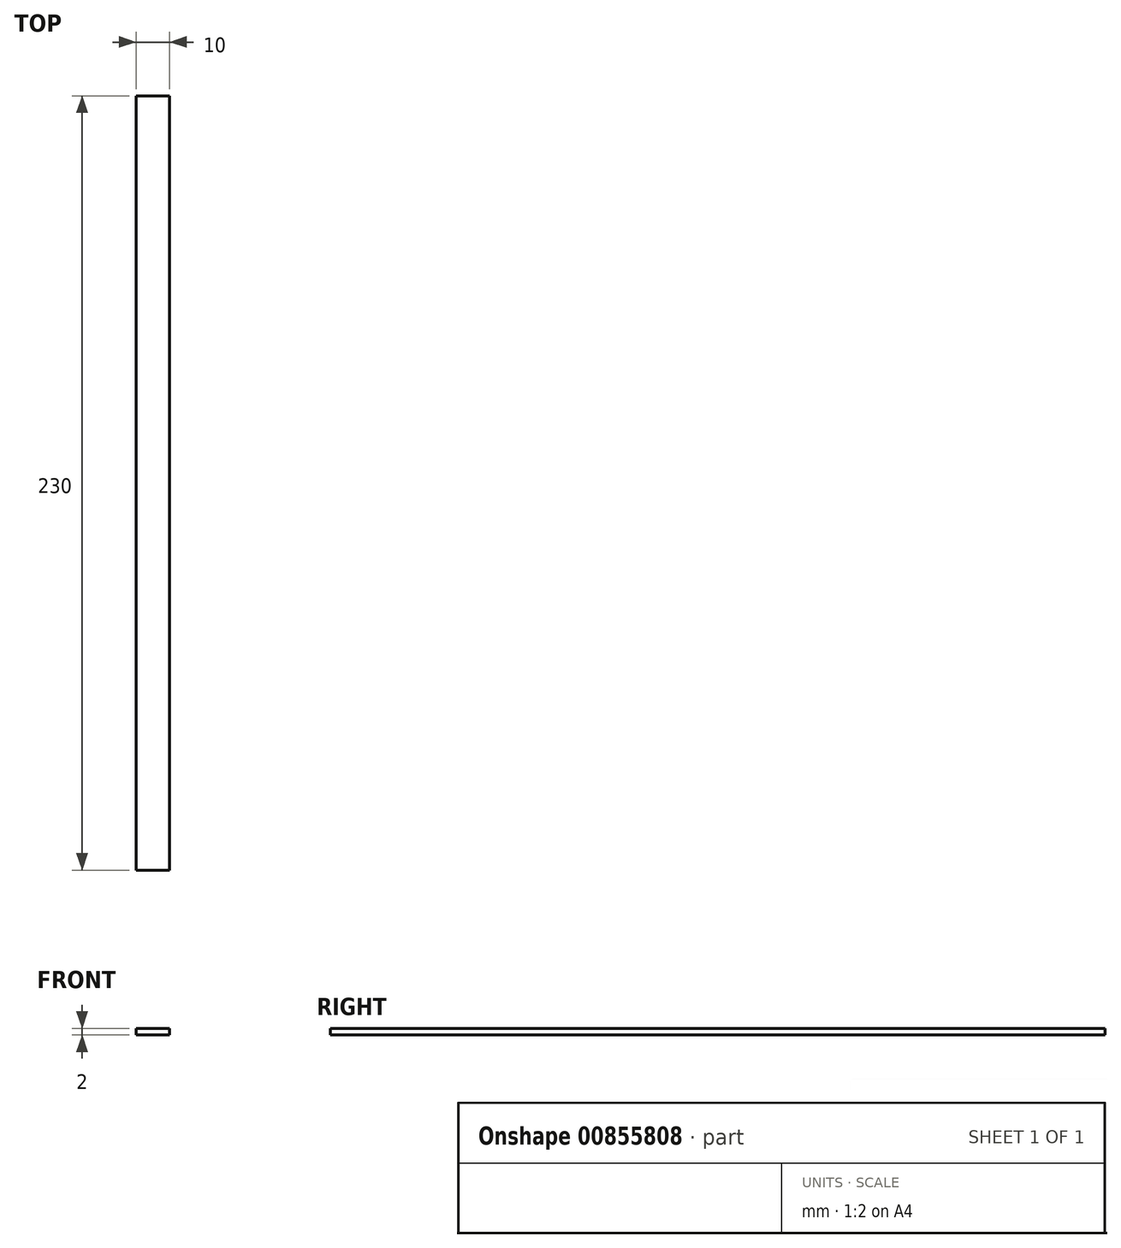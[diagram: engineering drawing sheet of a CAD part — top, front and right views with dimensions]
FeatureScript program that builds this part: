
annotation { "Feature Type Name" : "Feature", "Feature Type Description" : "" }
export const myFeature = defineFeature(function(context is Context, id is Id, definition is map)
    precondition{}
    {
        {
            var Q0;
            Q0=qCreatedBy(makeId("Front.planeOp"),FACE);
            var sketch = newSketch(context, id + "F0", { "sketchPlane" : qUnion([Q0])});
            skLineSegment(sketch, "E0.bottom", {"start": v(5, 1) * mm, "end": v(-5, 1) * mm});
            skLineSegment(sketch, "E0.top", {"start": v(5, -1) * mm, "end": v(-5, -1) * mm});
            skLineSegment(sketch, "E0.left", {"start": v(5, 1) * mm, "end": v(5, -1) * mm});
            skLineSegment(sketch, "E0.right", {"start": v(-5, 1) * mm, "end": v(-5, -1) * mm});
            skPoint(sketch, "E0.middle", {"position": v(0, 0) * mm});
            skSolve(sketch);
        }
        {
            var Q0;
            Q0 = qSketchRegion(id + "F0", true);
            extrude(context, id + "F1", {"entities" : qUnion([Q0]), "depth" : 230 * mm, "offsetDistance" : 25 * mm});
        }
    });
